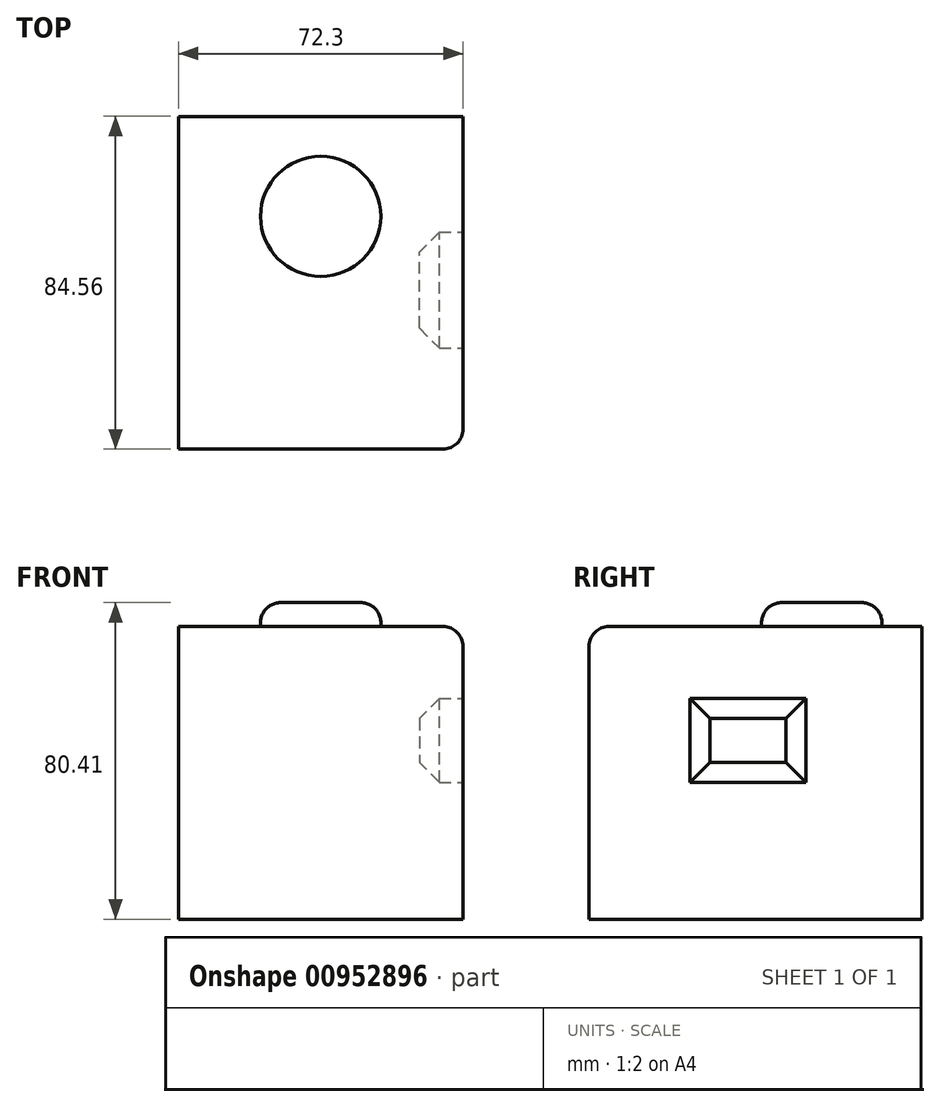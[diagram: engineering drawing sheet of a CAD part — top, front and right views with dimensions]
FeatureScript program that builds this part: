
annotation { "Feature Type Name" : "Feature", "Feature Type Description" : "" }
export const myFeature = defineFeature(function(context is Context, id is Id, definition is map)
    precondition{}
    {
        {
            var Q0;
            Q0=qCreatedBy(makeId("Top.planeOp"),FACE);
            var sketch = newSketch(context, id + "F0", { "sketchPlane" : qUnion([Q0])});
            skLineSegment(sketch, "E0.bottom", {"start": v(36.15, 42.28) * mm, "end": v(-36.15, 42.28) * mm});
            skLineSegment(sketch, "E0.top", {"start": v(36.15, -42.28) * mm, "end": v(-36.15, -42.28) * mm});
            skLineSegment(sketch, "E0.left", {"start": v(36.15, 42.28) * mm, "end": v(36.15, -42.28) * mm});
            skLineSegment(sketch, "E0.right", {"start": v(-36.15, 42.28) * mm, "end": v(-36.15, -42.28) * mm});
            skPoint(sketch, "E0.middle", {"position": v(0, 0) * mm});
            skSolve(sketch);
        }
        {
            var Q0;
            Q0=makeQuery(id+"F0.imprint","IMPRINT",FACE,{"disambiguationData":[TD([[makeQuery(id+"F0.imprint","IMPRINT",EDGE,{"derivedFrom":sQuery(id+"F0.wireOp",EDGE,"E0.bottom")}),1.0]])]});
            extrude(context, id + "F1", {"entities" : qUnion([Q0]), "depth" : 74.34 * mm, "offsetDistance" : 25.4 * mm});
        }
        {
            var Q0;
            Q0=makeQuery(id+"F1.opExtrude","CAP_FACE",FACE,{"disambiguationData":[OSD([sQuery(id+"F0.wireOp",EDGE,"E0.bottom"),sQuery(id+"F0.wireOp",EDGE,"E0.top"),sQuery(id+"F0.wireOp",EDGE,"E0.left"),sQuery(id+"F0.wireOp",EDGE,"E0.right")])],"isStart":false});
            var sketch = newSketch(context, id + "F2", { "sketchPlane" : qUnion([Q0])});
            skCircle(sketch, "E1", {"center": v(0, 16.86) * mm, "radius": 15.28 * mm});
            skSolve(sketch);
        }
        {
            var Q0;
            Q0=makeQuery(id+"F2.imprint","IMPRINT",FACE,{"disambiguationData":[TD([[makeQuery(id+"F2.imprint","IMPRINT",EDGE,{"derivedFrom":sQuery(id+"F2.wireOp",EDGE,"E1")}),1.0]])]});
            extrude(context, id + "F3", {"entities" : qUnion([Q0]), "operationType" : NewBodyOperationType.ADD, "depth" : 6.08 * mm, "offsetDistance" : 25.4 * mm});
        }
        {
            var Q0;
            Q0=makeQuery(id+"F3.opExtrude","CAP_EDGE",EDGE,{"disambiguationData":[OSD([sQuery(id+"F2.wireOp",EDGE,"E1")])],"isStart":false});
            var Q1;
            Q1=makeQuery(id+"F3.opExtrude","CAP_FACE",FACE,{"disambiguationData":[OSD([sQuery(id+"F2.wireOp",EDGE,"E1")])],"isStart":false});
            var Q2;
            Q2=makeQuery(id+"F1.opExtrude","CAP_EDGE",EDGE,{"disambiguationData":[OSD([sQuery(id+"F0.wireOp",EDGE,"E0.top")])],"isStart":false});
            var Q3;
            Q3=makeQuery(id+"F1.opExtrude","CAP_EDGE",EDGE,{"disambiguationData":[OSD([sQuery(id+"F0.wireOp",EDGE,"E0.left")])],"isStart":false});
            var Q4;
            Q4=makeQuery(id+"F1.opExtrude","SWEPT_EDGE",EDGE,{"disambiguationData":[OSD([sQuery(id+"F0.wireOp",EDGE,"E0.top"),sQuery(id+"F0.wireOp",EDGE,"E0.left")])]});
            fillet(context, id + "F4", {"entities" : qUnion([Q0, Q1, Q2, Q3, Q4]), "radius" : 5.08 * mm, "tangentPropagation" : true, "allowEdgeOverflow" : false});
        }
        {
            var Q0;
            Q0=makeQuery(id+"F1.opExtrude","SWEPT_FACE",FACE,{"disambiguationData":[OSD([sQuery(id+"F0.wireOp",EDGE,"E0.left")])]});
            var sketch = newSketch(context, id + "F5", { "sketchPlane" : qUnion([Q0])});
            skLineSegment(sketch, "E2.bottom", {"start": v(-16.57, 56.06) * mm, "end": v(12.85, 56.06) * mm});
            skLineSegment(sketch, "E2.top", {"start": v(-16.57, 34.75) * mm, "end": v(12.85, 34.75) * mm});
            skLineSegment(sketch, "E2.left", {"start": v(-16.57, 56.06) * mm, "end": v(-16.57, 34.75) * mm});
            skLineSegment(sketch, "E2.right", {"start": v(12.85, 56.06) * mm, "end": v(12.85, 34.75) * mm});
            skSolve(sketch);
        }
        {
            var Q0;
            Q0=makeQuery(id+"F5.imprint","IMPRINT",FACE,{"disambiguationData":[TD([[makeQuery(id+"F5.imprint","IMPRINT",EDGE,{"derivedFrom":sQuery(id+"F5.wireOp",EDGE,"E2.bottom")}),-1.0]])]});
            extrude(context, id + "F6", {"entities" : qUnion([Q0]), "operationType" : NewBodyOperationType.REMOVE, "oppositeDirection" : true, "depth" : 11.1 * mm, "offsetDistance" : 25.4 * mm});
        }
        {
            var Q0;
            Q0=makeQuery(id+"F6.boolean.opBoolean","COPY",EDGE,{"derivedFrom":makeQuery(id+"F6.opExtrude","CAP_EDGE",EDGE,{"disambiguationData":[OSD([sQuery(id+"F5.wireOp",EDGE,"E2.bottom")])],"isStart":false})});
            var Q1;
            Q1=makeQuery(id+"F6.boolean.opBoolean","COPY",EDGE,{"derivedFrom":makeQuery(id+"F6.opExtrude","CAP_EDGE",EDGE,{"disambiguationData":[OSD([sQuery(id+"F5.wireOp",EDGE,"E2.left")])],"isStart":false})});
            var Q2;
            Q2=makeQuery(id+"F6.boolean.opBoolean","COPY",EDGE,{"derivedFrom":makeQuery(id+"F6.opExtrude","CAP_EDGE",EDGE,{"disambiguationData":[OSD([sQuery(id+"F5.wireOp",EDGE,"E2.top")])],"isStart":false})});
            var Q3;
            Q3=makeQuery(id+"F6.boolean.opBoolean","COPY",EDGE,{"derivedFrom":makeQuery(id+"F6.opExtrude","CAP_EDGE",EDGE,{"disambiguationData":[OSD([sQuery(id+"F5.wireOp",EDGE,"E2.right")])],"isStart":false})});
            chamfer(context, id + "F7", {"entities" : qUnion([Q0, Q1, Q2, Q3]), "width" : 5.08 * mm, "tangentPropagation" : true});
        }
    });
